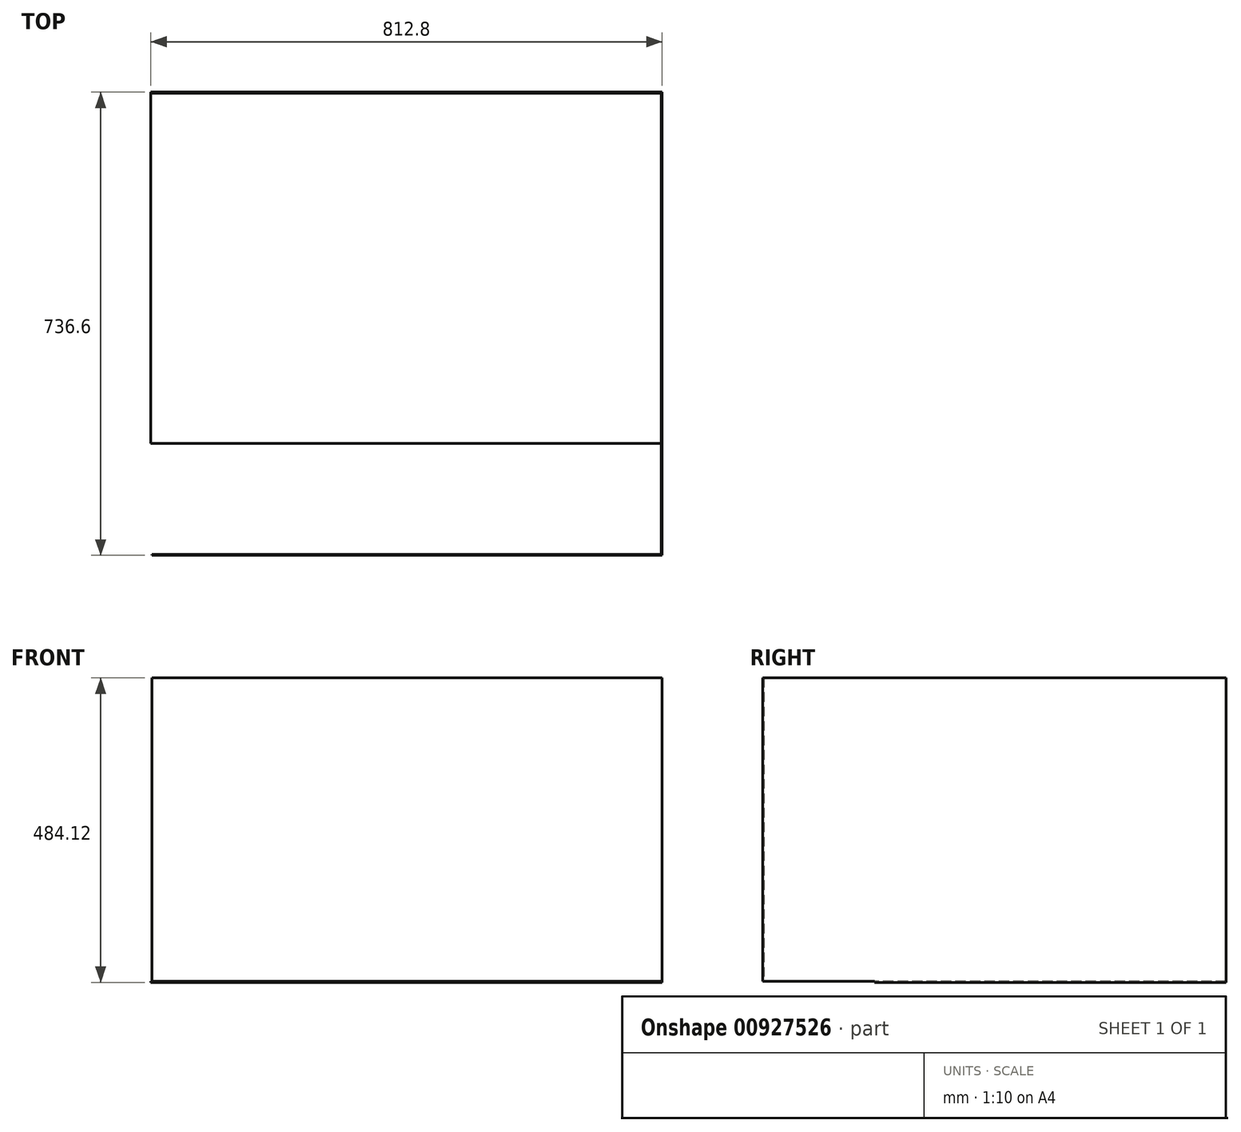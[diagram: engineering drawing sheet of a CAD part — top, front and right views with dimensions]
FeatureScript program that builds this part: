
annotation { "Feature Type Name" : "Feature", "Feature Type Description" : "" }
export const myFeature = defineFeature(function(context is Context, id is Id, definition is map)
    precondition{}
    {
        {
            var Q0;
            Q0=qCreatedBy(makeId("Top.planeOp"),FACE);
            var sketch = newSketch(context, id + "F0", { "sketchPlane" : qUnion([Q0])});
            skLineSegment(sketch, "E0.bottom", {"start": v(-419.43, 184.79) * mm, "end": v(393.37, 184.79) * mm});
            skLineSegment(sketch, "E0.top", {"start": v(-419.43, -297.81) * mm, "end": v(393.37, -297.81) * mm});
            skLineSegment(sketch, "E0.left", {"start": v(-419.43, 184.79) * mm, "end": v(-419.43, -297.81) * mm});
            skLineSegment(sketch, "E0.right", {"start": v(393.37, 184.79) * mm, "end": v(393.37, -297.81) * mm});
            skSolve(sketch);
        }
        {
            var Q0;
            Q0=qSketchRegion(id+"F0",true);
            var Q1;
            Q1=makeQuery(id+"F0.imprint","IMPRINT",FACE,{"disambiguationData":[TD([[makeQuery(id+"F0.imprint","IMPRINT",EDGE,{"derivedFrom":sQuery(id+"F0.wireOp",EDGE,"E0.bottom")}),-1.0]])]});
            extrude(context, id + "F1", {"entities" : qUnion([Q0, Q1]), "depth" : 1.52 * mm, "offsetDistance" : 25.4 * mm});
        }
        {
            var Q0;
            Q0=makeQuery(id+"F1.opExtrude","CAP_FACE",FACE,{"disambiguationData":[OSD([sQuery(id+"F0.wireOp",EDGE,"E0.bottom"),sQuery(id+"F0.wireOp",EDGE,"E0.top"),sQuery(id+"F0.wireOp",EDGE,"E0.left"),sQuery(id+"F0.wireOp",EDGE,"E0.right")])],"isStart":false});
            var sketch = newSketch(context, id + "F2", { "sketchPlane" : qUnion([Q0])});
            skLineSegment(sketch, "E1.bottom", {"start": v(-419.43, 184.79) * mm, "end": v(-417.91, 184.79) * mm});
            skLineSegment(sketch, "E1.top", {"start": v(-419.43, -297.81) * mm, "end": v(-417.91, -297.81) * mm});
            skLineSegment(sketch, "E1.left", {"start": v(-419.43, 184.79) * mm, "end": v(-419.43, -297.81) * mm});
            skLineSegment(sketch, "E2.left", {"start": v(-417.91, 184.79) * mm, "end": v(-417.91, 183.27) * mm});
            skLineSegment(sketch, "E3.bottom", {"start": v(393.37, 184.79) * mm, "end": v(391.84, 184.79) * mm});
            skLineSegment(sketch, "E3.top", {"start": v(393.37, -297.81) * mm, "end": v(391.84, -297.81) * mm});
            skLineSegment(sketch, "E3.left", {"start": v(393.37, 184.79) * mm, "end": v(393.37, -297.81) * mm});
            skLineSegment(sketch, "E3.right", {"start": v(391.84, 184.79) * mm, "end": v(391.84, -297.81) * mm});
            skLineSegment(sketch, "E4.bottom", {"start": v(-417.91, 184.79) * mm, "end": v(391.84, 184.79) * mm});
            skLineSegment(sketch, "E4.top", {"start": v(-417.91, 183.27) * mm, "end": v(391.84, 183.27) * mm});
            skLineSegment(sketch, "E4.right", {"start": v(391.84, 184.79) * mm, "end": v(391.84, 183.27) * mm});
            skLineSegment(sketch, "E5.bottom", {"start": v(-417.91, -297.81) * mm, "end": v(391.84, -297.81) * mm});
            skLineSegment(sketch, "E5.top", {"start": v(-417.91, -296.29) * mm, "end": v(391.84, -296.29) * mm});
            skLineSegment(sketch, "E5.left", {"start": v(-417.91, -297.81) * mm, "end": v(-417.91, -296.29) * mm});
            skLineSegment(sketch, "E5.right", {"start": v(391.84, -297.81) * mm, "end": v(391.84, -296.29) * mm});
            skLineSegment(sketch, "E6.bottom", {"start": v(-417.91, 184.79) * mm, "end": v(-419.43, 184.79) * mm});
            skLineSegment(sketch, "E6.top", {"start": v(-417.91, -297.81) * mm, "end": v(-419.43, -297.81) * mm});
            skLineSegment(sketch, "E6.left", {"start": v(-417.91, 184.79) * mm, "end": v(-417.91, -297.81) * mm});
            skSolve(sketch);
        }
        {
            var Q0;
            Q0=makeQuery(id+"F2.imprint","IMPRINT",FACE,{"disambiguationData":[TD([[makeQuery(id+"F2.imprint","IMPRINT",EDGE,{"derivedFrom":sQuery(id+"F2.wireOp",EDGE,"E3.bottom")}),-1.0]])]});
            var Q1;
            {var subQ0=sQuery(id+"F2.wireOp",EDGE,"E4.bottom");Q1=makeQuery(id+"F2.imprint","IMPRINT",FACE,{"disambiguationData":[TD([[makeQuery(id+"F2.imprint","IMPRINT",EDGE,{"derivedFrom":subQ0}),-1.0]])]});}
            var Q2;
            {var subQ0=sQuery(id+"F2.wireOp",EDGE,"E5.bottom");Q2=makeQuery(id+"F2.imprint","IMPRINT",FACE,{"disambiguationData":[TD([[makeQuery(id+"F2.imprint","IMPRINT",EDGE,{"derivedFrom":subQ0}),1.0]])]});}
            var Q3;
            {var subQ3=sQuery(id+"F2.wireOp",EDGE,"E6.bottom");Q3=makeQuery(id+"F2.imprint","IMPRINT",FACE,{"disambiguationData":[TD([[makeQuery(id+"F2.imprint","IMPRINT",EDGE,{"derivedFrom":subQ3}),-1.0]])]});}
            extrude(context, id + "F3", {"entities" : qUnion([Q0, Q1, Q2, Q3]), "operationType" : NewBodyOperationType.ADD, "depth" : 482.6 * mm, "offsetDistance" : 25.4 * mm});
        }
        {
            var Q0;
            Q0=makeQuery(id+"F3.boolean.opBoolean","MERGE",FACE,{"derivedFrom":[makeQuery(id+"F1.opExtrude","SWEPT_FACE",FACE,{"disambiguationData":[OSD([sQuery(id+"F0.wireOp",EDGE,"E0.top")])]}),makeQuery(id+"F3.opExtrude","SWEPT_FACE",FACE,{"disambiguationData":[OSD([sQuery(id+"F2.wireOp",EDGE,"E3.top"),sQuery(id+"F2.wireOp",EDGE,"E5.bottom"),sQuery(id+"F2.wireOp",EDGE,"E6.top")])]})]});
            extrude(context, id + "F4", {"entities" : qUnion([Q0]), "operationType" : NewBodyOperationType.ADD, "depth" : 254 * mm, "offsetDistance" : 25.4 * mm});
        }
        {
            var Q0;
            Q0=makeQuery(id+"F3.opExtrude","SWEPT_FACE",FACE,{"disambiguationData":[OSD([sQuery(id+"F2.wireOp",EDGE,"E5.top")])]});
            extrude(context, id + "F5", {"entities" : qUnion([Q0]), "operationType" : NewBodyOperationType.REMOVE, "oppositeDirection" : true, "depth" : 254 * mm, "offsetDistance" : 25.4 * mm});
        }
        {
            var Q0;
            {var subQ0=sQuery(id+"F0.wireOp",EDGE,"E0.top");Q0=makeQuery(id+"F4.boolean.opBoolean","MERGE",FACE,{"derivedFrom":[makeQuery(id+"F1.opExtrude","CAP_FACE",FACE,{"disambiguationData":[OSD([sQuery(id+"F0.wireOp",EDGE,"E0.bottom"),subQ0,sQuery(id+"F0.wireOp",EDGE,"E0.left"),sQuery(id+"F0.wireOp",EDGE,"E0.right")])],"isStart":true}),makeQuery(id+"F4.opExtrude","SWEPT_FACE",FACE,{"disambiguationData":[OSD([subQ0])]})]});}
            var sketch = newSketch(context, id + "F6", { "sketchPlane" : qUnion([Q0])});
            skLineSegment(sketch, "E7.bottom", {"start": v(-419.43, 551.81) * mm, "end": v(393.37, 551.81) * mm});
            skLineSegment(sketch, "E7.top", {"start": v(-419.43, 374.01) * mm, "end": v(393.37, 374.01) * mm});
            skLineSegment(sketch, "E7.left", {"start": v(-419.43, 551.81) * mm, "end": v(-419.43, 374.01) * mm});
            skLineSegment(sketch, "E7.right", {"start": v(393.37, 551.81) * mm, "end": v(393.37, 374.01) * mm});
            skSolve(sketch);
        }
        {
            var Q0;
            Q0=makeQuery(id+"F6.imprint","IMPRINT",FACE,{"disambiguationData":[TD([[makeQuery(id+"F6.imprint","IMPRINT",EDGE,{"derivedFrom":sQuery(id+"F6.wireOp",EDGE,"E7.bottom")}),-1.0]])]});
            extrude(context, id + "F7", {"entities" : qUnion([Q0]), "operationType" : NewBodyOperationType.REMOVE, "oppositeDirection" : true, "depth" : 1.52 * mm, "offsetDistance" : 25.4 * mm});
        }
    });
